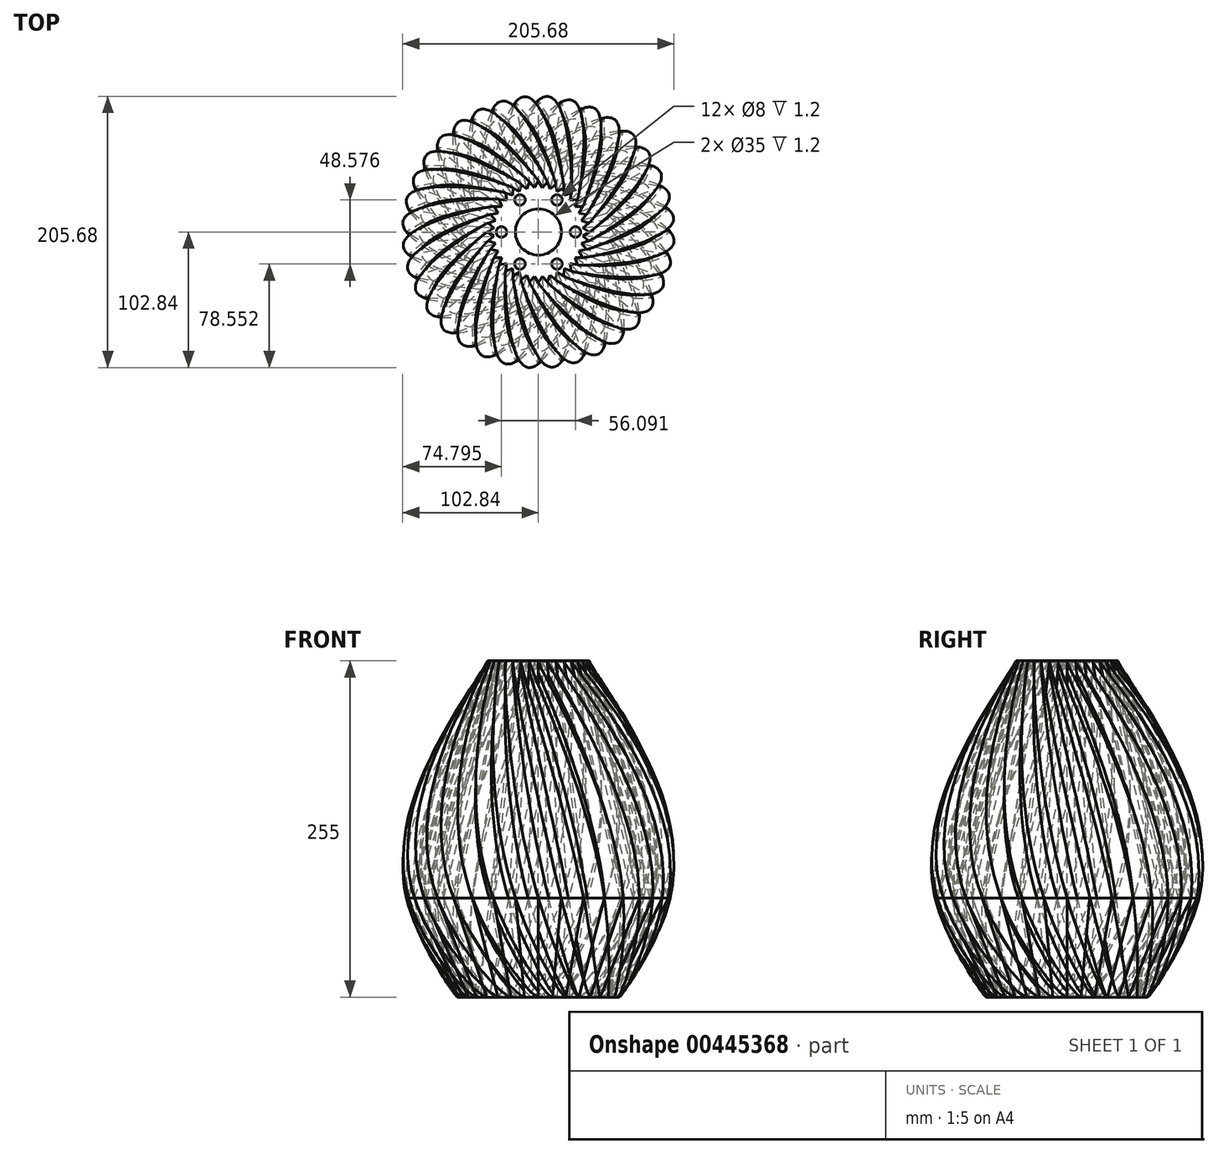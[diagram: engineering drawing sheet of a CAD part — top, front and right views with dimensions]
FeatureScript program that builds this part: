
annotation { "Feature Type Name" : "Feature", "Feature Type Description" : "" }
export const myFeature = defineFeature(function(context is Context, id is Id, definition is map)
    precondition{}
    {
        {
            var Q0;
            Q0=qCreatedBy(makeId("Top.planeOp"),FACE);
            var sketch = newSketch(context, id + "F0", { "sketchPlane" : qUnion([Q0])});
            skCircle(sketch, "E0", {"center": v(0, 0) * mm, "radius": 100 * mm, "construction": true});
            skLineSegment(sketch, "E1", {"start": v(-7.64, 87.34) * mm, "end": v(0, 100) * mm});
            skLineSegment(sketch, "E2.MirrorCS", {"start": v(7.64, 87.34) * mm, "end": v(0, 100) * mm});
            skLineSegment(sketch, "E3.1.0", {"start": v(-22.7, 84.69) * mm, "end": v(-17.36, 98.48) * mm});
            skLineSegment(sketch, "E3.1.1", {"start": v(-7.64, 87.34) * mm, "end": v(-17.36, 98.48) * mm});
            skLineSegment(sketch, "E3.2.0", {"start": v(-37.05, 79.46) * mm, "end": v(-34.2, 93.97) * mm});
            skLineSegment(sketch, "E3.2.1", {"start": v(-22.7, 84.69) * mm, "end": v(-34.2, 93.97) * mm});
            skLineSegment(sketch, "E3.3.0", {"start": v(-50.29, 71.82) * mm, "end": v(-50, 86.6) * mm});
            skLineSegment(sketch, "E3.3.1", {"start": v(-37.05, 79.46) * mm, "end": v(-50, 86.6) * mm});
            skLineSegment(sketch, "E3.4.0", {"start": v(-62, 62) * mm, "end": v(-64.28, 76.6) * mm});
            skLineSegment(sketch, "E3.4.1", {"start": v(-50.29, 71.82) * mm, "end": v(-64.28, 76.6) * mm});
            skLineSegment(sketch, "E3.5.0", {"start": v(-71.82, 50.29) * mm, "end": v(-76.6, 64.28) * mm});
            skLineSegment(sketch, "E3.5.1", {"start": v(-62, 62) * mm, "end": v(-76.6, 64.28) * mm});
            skLineSegment(sketch, "E3.6.0", {"start": v(-79.46, 37.05) * mm, "end": v(-86.6, 50) * mm});
            skLineSegment(sketch, "E3.6.1", {"start": v(-71.82, 50.29) * mm, "end": v(-86.6, 50) * mm});
            skLineSegment(sketch, "E3.7.0", {"start": v(-84.69, 22.7) * mm, "end": v(-93.97, 34.2) * mm});
            skLineSegment(sketch, "E3.7.1", {"start": v(-79.46, 37.05) * mm, "end": v(-93.97, 34.2) * mm});
            skLineSegment(sketch, "E3.8.0", {"start": v(-87.34, 7.64) * mm, "end": v(-98.48, 17.36) * mm});
            skLineSegment(sketch, "E3.8.1", {"start": v(-84.69, 22.7) * mm, "end": v(-98.48, 17.36) * mm});
            skLineSegment(sketch, "E3.9.0", {"start": v(-87.34, -7.64) * mm, "end": v(-100, 0) * mm});
            skLineSegment(sketch, "E3.9.1", {"start": v(-87.34, 7.64) * mm, "end": v(-100, 0) * mm});
            skLineSegment(sketch, "E3.10.0", {"start": v(-84.69, -22.7) * mm, "end": v(-98.48, -17.36) * mm});
            skLineSegment(sketch, "E3.10.1", {"start": v(-87.34, -7.64) * mm, "end": v(-98.48, -17.36) * mm});
            skLineSegment(sketch, "E3.11.0", {"start": v(-79.46, -37.05) * mm, "end": v(-93.97, -34.2) * mm});
            skLineSegment(sketch, "E3.11.1", {"start": v(-84.69, -22.7) * mm, "end": v(-93.97, -34.2) * mm});
            skLineSegment(sketch, "E3.12.0", {"start": v(-71.82, -50.29) * mm, "end": v(-86.6, -50) * mm});
            skLineSegment(sketch, "E3.12.1", {"start": v(-79.46, -37.05) * mm, "end": v(-86.6, -50) * mm});
            skLineSegment(sketch, "E3.13.0", {"start": v(-62, -62) * mm, "end": v(-76.6, -64.28) * mm});
            skLineSegment(sketch, "E3.13.1", {"start": v(-71.82, -50.29) * mm, "end": v(-76.6, -64.28) * mm});
            skLineSegment(sketch, "E3.14.0", {"start": v(-50.29, -71.82) * mm, "end": v(-64.28, -76.6) * mm});
            skLineSegment(sketch, "E3.14.1", {"start": v(-62, -62) * mm, "end": v(-64.28, -76.6) * mm});
            skLineSegment(sketch, "E3.15.0", {"start": v(-37.05, -79.46) * mm, "end": v(-50, -86.6) * mm});
            skLineSegment(sketch, "E3.15.1", {"start": v(-50.29, -71.82) * mm, "end": v(-50, -86.6) * mm});
            skLineSegment(sketch, "E3.16.0", {"start": v(-22.7, -84.69) * mm, "end": v(-34.2, -93.97) * mm});
            skLineSegment(sketch, "E3.16.1", {"start": v(-37.05, -79.46) * mm, "end": v(-34.2, -93.97) * mm});
            skLineSegment(sketch, "E3.17.0", {"start": v(-7.64, -87.34) * mm, "end": v(-17.36, -98.48) * mm});
            skLineSegment(sketch, "E3.17.1", {"start": v(-22.7, -84.69) * mm, "end": v(-17.36, -98.48) * mm});
            skLineSegment(sketch, "E3.18.0", {"start": v(7.64, -87.34) * mm, "end": v(0, -100) * mm});
            skLineSegment(sketch, "E3.18.1", {"start": v(-7.64, -87.34) * mm, "end": v(0, -100) * mm});
            skLineSegment(sketch, "E3.19.0", {"start": v(22.7, -84.69) * mm, "end": v(17.36, -98.48) * mm});
            skLineSegment(sketch, "E3.19.1", {"start": v(7.64, -87.34) * mm, "end": v(17.36, -98.48) * mm});
            skLineSegment(sketch, "E3.20.0", {"start": v(37.05, -79.46) * mm, "end": v(34.2, -93.97) * mm});
            skLineSegment(sketch, "E3.20.1", {"start": v(22.7, -84.69) * mm, "end": v(34.2, -93.97) * mm});
            skLineSegment(sketch, "E3.21.0", {"start": v(50.29, -71.82) * mm, "end": v(50, -86.6) * mm});
            skLineSegment(sketch, "E3.21.1", {"start": v(37.05, -79.46) * mm, "end": v(50, -86.6) * mm});
            skLineSegment(sketch, "E3.22.0", {"start": v(62, -62) * mm, "end": v(64.28, -76.6) * mm});
            skLineSegment(sketch, "E3.22.1", {"start": v(50.29, -71.82) * mm, "end": v(64.28, -76.6) * mm});
            skLineSegment(sketch, "E3.23.0", {"start": v(71.82, -50.29) * mm, "end": v(76.6, -64.28) * mm});
            skLineSegment(sketch, "E3.23.1", {"start": v(62, -62) * mm, "end": v(76.6, -64.28) * mm});
            skLineSegment(sketch, "E3.24.0", {"start": v(79.46, -37.05) * mm, "end": v(86.6, -50) * mm});
            skLineSegment(sketch, "E3.24.1", {"start": v(71.82, -50.29) * mm, "end": v(86.6, -50) * mm});
            skLineSegment(sketch, "E3.25.0", {"start": v(84.69, -22.7) * mm, "end": v(93.97, -34.2) * mm});
            skLineSegment(sketch, "E3.25.1", {"start": v(79.46, -37.05) * mm, "end": v(93.97, -34.2) * mm});
            skLineSegment(sketch, "E3.26.0", {"start": v(87.34, -7.64) * mm, "end": v(98.48, -17.36) * mm});
            skLineSegment(sketch, "E3.26.1", {"start": v(84.69, -22.7) * mm, "end": v(98.48, -17.36) * mm});
            skLineSegment(sketch, "E3.27.0", {"start": v(87.34, 7.64) * mm, "end": v(100, 0) * mm});
            skLineSegment(sketch, "E3.27.1", {"start": v(87.34, -7.64) * mm, "end": v(100, 0) * mm});
            skLineSegment(sketch, "E3.28.0", {"start": v(84.69, 22.7) * mm, "end": v(98.48, 17.36) * mm});
            skLineSegment(sketch, "E3.28.1", {"start": v(87.34, 7.64) * mm, "end": v(98.48, 17.36) * mm});
            skLineSegment(sketch, "E3.29.0", {"start": v(79.46, 37.05) * mm, "end": v(93.97, 34.2) * mm});
            skLineSegment(sketch, "E3.29.1", {"start": v(84.69, 22.7) * mm, "end": v(93.97, 34.2) * mm});
            skLineSegment(sketch, "E3.30.0", {"start": v(71.82, 50.29) * mm, "end": v(86.6, 50) * mm});
            skLineSegment(sketch, "E3.30.1", {"start": v(79.46, 37.05) * mm, "end": v(86.6, 50) * mm});
            skLineSegment(sketch, "E3.31.0", {"start": v(62, 62) * mm, "end": v(76.6, 64.28) * mm});
            skLineSegment(sketch, "E3.31.1", {"start": v(71.82, 50.29) * mm, "end": v(76.6, 64.28) * mm});
            skLineSegment(sketch, "E3.32.0", {"start": v(50.29, 71.82) * mm, "end": v(64.28, 76.6) * mm});
            skLineSegment(sketch, "E3.32.1", {"start": v(62, 62) * mm, "end": v(64.28, 76.6) * mm});
            skLineSegment(sketch, "E3.33.0", {"start": v(37.05, 79.46) * mm, "end": v(50, 86.6) * mm});
            skLineSegment(sketch, "E3.33.1", {"start": v(50.29, 71.82) * mm, "end": v(50, 86.6) * mm});
            skLineSegment(sketch, "E3.34.0", {"start": v(22.7, 84.69) * mm, "end": v(34.2, 93.97) * mm});
            skLineSegment(sketch, "E3.34.1", {"start": v(37.05, 79.46) * mm, "end": v(34.2, 93.97) * mm});
            skLineSegment(sketch, "E3.35.0", {"start": v(7.64, 87.34) * mm, "end": v(17.36, 98.48) * mm});
            skLineSegment(sketch, "E3.35.1", {"start": v(22.7, 84.69) * mm, "end": v(17.36, 98.48) * mm});
            skSolve(sketch);
        }
        {
            var Q0;
            Q0=makeQuery(id+"F0.imprint","IMPRINT",FACE,{"disambiguationData":[TD([[makeQuery(id+"F0.imprint","IMPRINT",EDGE,{"derivedFrom":sQuery(id+"F0.wireOp",EDGE,"E1")}),-1.0]])]});
            extrude(context, id + "F1", {"entities" : qUnion([Q0]), "depth" : 180 * mm, "hasDraft" : true, "draftAngle" : 10 * degree, "draftPullDirection" : true});
        }
        {
            var Q1;
            Q1=makeQuery(id+"F1.opExtrude","CAP_FACE",FACE,{"disambiguationData":[OSD([sQuery(id+"F0.wireOp",EDGE,"E1"),sQuery(id+"F0.wireOp",EDGE,"E2.MirrorCS"),sQuery(id+"F0.wireOp",EDGE,"E3.1.0"),sQuery(id+"F0.wireOp",EDGE,"E3.1.1"),sQuery(id+"F0.wireOp",EDGE,"E3.2.0"),sQuery(id+"F0.wireOp",EDGE,"E3.2.1"),sQuery(id+"F0.wireOp",EDGE,"E3.3.0"),sQuery(id+"F0.wireOp",EDGE,"E3.3.1"),sQuery(id+"F0.wireOp",EDGE,"E3.4.0"),sQuery(id+"F0.wireOp",EDGE,"E3.4.1"),sQuery(id+"F0.wireOp",EDGE,"E3.5.0"),sQuery(id+"F0.wireOp",EDGE,"E3.5.1"),sQuery(id+"F0.wireOp",EDGE,"E3.6.0"),sQuery(id+"F0.wireOp",EDGE,"E3.6.1"),sQuery(id+"F0.wireOp",EDGE,"E3.7.0"),sQuery(id+"F0.wireOp",EDGE,"E3.7.1"),sQuery(id+"F0.wireOp",EDGE,"E3.8.0"),sQuery(id+"F0.wireOp",EDGE,"E3.8.1"),sQuery(id+"F0.wireOp",EDGE,"E3.9.0"),sQuery(id+"F0.wireOp",EDGE,"E3.9.1"),sQuery(id+"F0.wireOp",EDGE,"E3.10.0"),sQuery(id+"F0.wireOp",EDGE,"E3.10.1"),sQuery(id+"F0.wireOp",EDGE,"E3.11.0"),sQuery(id+"F0.wireOp",EDGE,"E3.11.1"),sQuery(id+"F0.wireOp",EDGE,"E3.12.0"),sQuery(id+"F0.wireOp",EDGE,"E3.12.1"),sQuery(id+"F0.wireOp",EDGE,"E3.13.0"),sQuery(id+"F0.wireOp",EDGE,"E3.13.1"),sQuery(id+"F0.wireOp",EDGE,"E3.14.0"),sQuery(id+"F0.wireOp",EDGE,"E3.14.1"),sQuery(id+"F0.wireOp",EDGE,"E3.15.0"),sQuery(id+"F0.wireOp",EDGE,"E3.15.1"),sQuery(id+"F0.wireOp",EDGE,"E3.16.0"),sQuery(id+"F0.wireOp",EDGE,"E3.16.1"),sQuery(id+"F0.wireOp",EDGE,"E3.17.0"),sQuery(id+"F0.wireOp",EDGE,"E3.17.1"),sQuery(id+"F0.wireOp",EDGE,"E3.18.0"),sQuery(id+"F0.wireOp",EDGE,"E3.18.1"),sQuery(id+"F0.wireOp",EDGE,"E3.19.0"),sQuery(id+"F0.wireOp",EDGE,"E3.19.1"),sQuery(id+"F0.wireOp",EDGE,"E3.20.0"),sQuery(id+"F0.wireOp",EDGE,"E3.20.1"),sQuery(id+"F0.wireOp",EDGE,"E3.21.0"),sQuery(id+"F0.wireOp",EDGE,"E3.21.1"),sQuery(id+"F0.wireOp",EDGE,"E3.22.0"),sQuery(id+"F0.wireOp",EDGE,"E3.22.1"),sQuery(id+"F0.wireOp",EDGE,"E3.23.0"),sQuery(id+"F0.wireOp",EDGE,"E3.23.1"),sQuery(id+"F0.wireOp",EDGE,"E3.24.0"),sQuery(id+"F0.wireOp",EDGE,"E3.24.1"),sQuery(id+"F0.wireOp",EDGE,"E3.25.0"),sQuery(id+"F0.wireOp",EDGE,"E3.25.1"),sQuery(id+"F0.wireOp",EDGE,"E3.26.0"),sQuery(id+"F0.wireOp",EDGE,"E3.26.1"),sQuery(id+"F0.wireOp",EDGE,"E3.27.0"),sQuery(id+"F0.wireOp",EDGE,"E3.27.1"),sQuery(id+"F0.wireOp",EDGE,"E3.28.0"),sQuery(id+"F0.wireOp",EDGE,"E3.28.1"),sQuery(id+"F0.wireOp",EDGE,"E3.29.0"),sQuery(id+"F0.wireOp",EDGE,"E3.29.1"),sQuery(id+"F0.wireOp",EDGE,"E3.30.0"),sQuery(id+"F0.wireOp",EDGE,"E3.30.1"),sQuery(id+"F0.wireOp",EDGE,"E3.31.0"),sQuery(id+"F0.wireOp",EDGE,"E3.31.1"),sQuery(id+"F0.wireOp",EDGE,"E3.32.0"),sQuery(id+"F0.wireOp",EDGE,"E3.32.1"),sQuery(id+"F0.wireOp",EDGE,"E3.33.0"),sQuery(id+"F0.wireOp",EDGE,"E3.33.1"),sQuery(id+"F0.wireOp",EDGE,"E3.34.0"),sQuery(id+"F0.wireOp",EDGE,"E3.34.1"),sQuery(id+"F0.wireOp",EDGE,"E3.35.0"),sQuery(id+"F0.wireOp",EDGE,"E3.35.1")])],"isStart":false});
            var Q2;
            Q2=makeQuery(id+"F1.opExtrude","CAP_FACE",FACE,{"disambiguationData":[OSD([sQuery(id+"F0.wireOp",EDGE,"E1"),sQuery(id+"F0.wireOp",EDGE,"E2.MirrorCS"),sQuery(id+"F0.wireOp",EDGE,"E3.1.0"),sQuery(id+"F0.wireOp",EDGE,"E3.1.1"),sQuery(id+"F0.wireOp",EDGE,"E3.2.0"),sQuery(id+"F0.wireOp",EDGE,"E3.2.1"),sQuery(id+"F0.wireOp",EDGE,"E3.3.0"),sQuery(id+"F0.wireOp",EDGE,"E3.3.1"),sQuery(id+"F0.wireOp",EDGE,"E3.4.0"),sQuery(id+"F0.wireOp",EDGE,"E3.4.1"),sQuery(id+"F0.wireOp",EDGE,"E3.5.0"),sQuery(id+"F0.wireOp",EDGE,"E3.5.1"),sQuery(id+"F0.wireOp",EDGE,"E3.6.0"),sQuery(id+"F0.wireOp",EDGE,"E3.6.1"),sQuery(id+"F0.wireOp",EDGE,"E3.7.0"),sQuery(id+"F0.wireOp",EDGE,"E3.7.1"),sQuery(id+"F0.wireOp",EDGE,"E3.8.0"),sQuery(id+"F0.wireOp",EDGE,"E3.8.1"),sQuery(id+"F0.wireOp",EDGE,"E3.9.0"),sQuery(id+"F0.wireOp",EDGE,"E3.9.1"),sQuery(id+"F0.wireOp",EDGE,"E3.10.0"),sQuery(id+"F0.wireOp",EDGE,"E3.10.1"),sQuery(id+"F0.wireOp",EDGE,"E3.11.0"),sQuery(id+"F0.wireOp",EDGE,"E3.11.1"),sQuery(id+"F0.wireOp",EDGE,"E3.12.0"),sQuery(id+"F0.wireOp",EDGE,"E3.12.1"),sQuery(id+"F0.wireOp",EDGE,"E3.13.0"),sQuery(id+"F0.wireOp",EDGE,"E3.13.1"),sQuery(id+"F0.wireOp",EDGE,"E3.14.0"),sQuery(id+"F0.wireOp",EDGE,"E3.14.1"),sQuery(id+"F0.wireOp",EDGE,"E3.15.0"),sQuery(id+"F0.wireOp",EDGE,"E3.15.1"),sQuery(id+"F0.wireOp",EDGE,"E3.16.0"),sQuery(id+"F0.wireOp",EDGE,"E3.16.1"),sQuery(id+"F0.wireOp",EDGE,"E3.17.0"),sQuery(id+"F0.wireOp",EDGE,"E3.17.1"),sQuery(id+"F0.wireOp",EDGE,"E3.18.0"),sQuery(id+"F0.wireOp",EDGE,"E3.18.1"),sQuery(id+"F0.wireOp",EDGE,"E3.19.0"),sQuery(id+"F0.wireOp",EDGE,"E3.19.1"),sQuery(id+"F0.wireOp",EDGE,"E3.20.0"),sQuery(id+"F0.wireOp",EDGE,"E3.20.1"),sQuery(id+"F0.wireOp",EDGE,"E3.21.0"),sQuery(id+"F0.wireOp",EDGE,"E3.21.1"),sQuery(id+"F0.wireOp",EDGE,"E3.22.0"),sQuery(id+"F0.wireOp",EDGE,"E3.22.1"),sQuery(id+"F0.wireOp",EDGE,"E3.23.0"),sQuery(id+"F0.wireOp",EDGE,"E3.23.1"),sQuery(id+"F0.wireOp",EDGE,"E3.24.0"),sQuery(id+"F0.wireOp",EDGE,"E3.24.1"),sQuery(id+"F0.wireOp",EDGE,"E3.25.0"),sQuery(id+"F0.wireOp",EDGE,"E3.25.1"),sQuery(id+"F0.wireOp",EDGE,"E3.26.0"),sQuery(id+"F0.wireOp",EDGE,"E3.26.1"),sQuery(id+"F0.wireOp",EDGE,"E3.27.0"),sQuery(id+"F0.wireOp",EDGE,"E3.27.1"),sQuery(id+"F0.wireOp",EDGE,"E3.28.0"),sQuery(id+"F0.wireOp",EDGE,"E3.28.1"),sQuery(id+"F0.wireOp",EDGE,"E3.29.0"),sQuery(id+"F0.wireOp",EDGE,"E3.29.1"),sQuery(id+"F0.wireOp",EDGE,"E3.30.0"),sQuery(id+"F0.wireOp",EDGE,"E3.30.1"),sQuery(id+"F0.wireOp",EDGE,"E3.31.0"),sQuery(id+"F0.wireOp",EDGE,"E3.31.1"),sQuery(id+"F0.wireOp",EDGE,"E3.32.0"),sQuery(id+"F0.wireOp",EDGE,"E3.32.1"),sQuery(id+"F0.wireOp",EDGE,"E3.33.0"),sQuery(id+"F0.wireOp",EDGE,"E3.33.1"),sQuery(id+"F0.wireOp",EDGE,"E3.34.0"),sQuery(id+"F0.wireOp",EDGE,"E3.34.1"),sQuery(id+"F0.wireOp",EDGE,"E3.35.0"),sQuery(id+"F0.wireOp",EDGE,"E3.35.1")])],"isStart":true});
            var Q3;
            Q3=makeQuery(id+"F1.opExtrude","CAP_VERTEX",VERTEX,{"disambiguationData":[OSD([sQuery(id+"F0.wireOp",EDGE,"E3.18.0"),sQuery(id+"F0.wireOp",EDGE,"E3.18.1")])],"isStart":true});
            var Q4;
            Q4=makeQuery(id+"F1.opExtrude","CAP_VERTEX",VERTEX,{"disambiguationData":[OSD([sQuery(id+"F0.wireOp",EDGE,"E3.22.0"),sQuery(id+"F0.wireOp",EDGE,"E3.22.1")])],"isStart":false});
            loft(context, id + "F2", {"endCondition" : LoftEndDerivativeType.NORMAL_TO_PROFILE, "endMagnitude" : 2, "sheetProfilesArray" : [{ "sheetProfileEntities" : qUnion([Q1]) }, { "sheetProfileEntities" : qUnion([Q2]) }], "matchConnections" : true, "connections" : [{ "connectionEntities" : qUnion([Q3, Q4]), "connectionEdgeQueries" : qUnion([]), "connectionEdgeParameters" : [] }]});
        }
        {
            var Q0;
            Q0=makeQuery(id+"F2.opLoft","SWEPT_BODY",BODY,{"disambiguationData":[OSD([sQuery(id+"F0.wireOp",EDGE,"E1"),sQuery(id+"F0.wireOp",EDGE,"E2.MirrorCS"),sQuery(id+"F0.wireOp",EDGE,"E3.1.0"),sQuery(id+"F0.wireOp",EDGE,"E3.1.1"),sQuery(id+"F0.wireOp",EDGE,"E3.2.0"),sQuery(id+"F0.wireOp",EDGE,"E3.2.1"),sQuery(id+"F0.wireOp",EDGE,"E3.3.0"),sQuery(id+"F0.wireOp",EDGE,"E3.3.1"),sQuery(id+"F0.wireOp",EDGE,"E3.4.0"),sQuery(id+"F0.wireOp",EDGE,"E3.4.1"),sQuery(id+"F0.wireOp",EDGE,"E3.5.0"),sQuery(id+"F0.wireOp",EDGE,"E3.5.1"),sQuery(id+"F0.wireOp",EDGE,"E3.6.0"),sQuery(id+"F0.wireOp",EDGE,"E3.6.1"),sQuery(id+"F0.wireOp",EDGE,"E3.7.0"),sQuery(id+"F0.wireOp",EDGE,"E3.7.1"),sQuery(id+"F0.wireOp",EDGE,"E3.8.0"),sQuery(id+"F0.wireOp",EDGE,"E3.8.1"),sQuery(id+"F0.wireOp",EDGE,"E3.9.0"),sQuery(id+"F0.wireOp",EDGE,"E3.9.1"),sQuery(id+"F0.wireOp",EDGE,"E3.10.0"),sQuery(id+"F0.wireOp",EDGE,"E3.10.1"),sQuery(id+"F0.wireOp",EDGE,"E3.11.0"),sQuery(id+"F0.wireOp",EDGE,"E3.11.1"),sQuery(id+"F0.wireOp",EDGE,"E3.12.0"),sQuery(id+"F0.wireOp",EDGE,"E3.12.1"),sQuery(id+"F0.wireOp",EDGE,"E3.13.0"),sQuery(id+"F0.wireOp",EDGE,"E3.13.1"),sQuery(id+"F0.wireOp",EDGE,"E3.14.0"),sQuery(id+"F0.wireOp",EDGE,"E3.14.1"),sQuery(id+"F0.wireOp",EDGE,"E3.15.0"),sQuery(id+"F0.wireOp",EDGE,"E3.15.1"),sQuery(id+"F0.wireOp",EDGE,"E3.16.0"),sQuery(id+"F0.wireOp",EDGE,"E3.16.1"),sQuery(id+"F0.wireOp",EDGE,"E3.17.0"),sQuery(id+"F0.wireOp",EDGE,"E3.17.1"),sQuery(id+"F0.wireOp",EDGE,"E3.18.0"),sQuery(id+"F0.wireOp",EDGE,"E3.18.1"),sQuery(id+"F0.wireOp",EDGE,"E3.19.0"),sQuery(id+"F0.wireOp",EDGE,"E3.19.1"),sQuery(id+"F0.wireOp",EDGE,"E3.20.0"),sQuery(id+"F0.wireOp",EDGE,"E3.20.1"),sQuery(id+"F0.wireOp",EDGE,"E3.21.0"),sQuery(id+"F0.wireOp",EDGE,"E3.21.1"),sQuery(id+"F0.wireOp",EDGE,"E3.22.0"),sQuery(id+"F0.wireOp",EDGE,"E3.22.1"),sQuery(id+"F0.wireOp",EDGE,"E3.23.0"),sQuery(id+"F0.wireOp",EDGE,"E3.23.1"),sQuery(id+"F0.wireOp",EDGE,"E3.24.0"),sQuery(id+"F0.wireOp",EDGE,"E3.24.1"),sQuery(id+"F0.wireOp",EDGE,"E3.25.0"),sQuery(id+"F0.wireOp",EDGE,"E3.25.1"),sQuery(id+"F0.wireOp",EDGE,"E3.26.0"),sQuery(id+"F0.wireOp",EDGE,"E3.26.1"),sQuery(id+"F0.wireOp",EDGE,"E3.27.0"),sQuery(id+"F0.wireOp",EDGE,"E3.27.1"),sQuery(id+"F0.wireOp",EDGE,"E3.28.0"),sQuery(id+"F0.wireOp",EDGE,"E3.28.1"),sQuery(id+"F0.wireOp",EDGE,"E3.29.0"),sQuery(id+"F0.wireOp",EDGE,"E3.29.1"),sQuery(id+"F0.wireOp",EDGE,"E3.30.0"),sQuery(id+"F0.wireOp",EDGE,"E3.30.1"),sQuery(id+"F0.wireOp",EDGE,"E3.31.0"),sQuery(id+"F0.wireOp",EDGE,"E3.31.1"),sQuery(id+"F0.wireOp",EDGE,"E3.32.0"),sQuery(id+"F0.wireOp",EDGE,"E3.32.1"),sQuery(id+"F0.wireOp",EDGE,"E3.33.0"),sQuery(id+"F0.wireOp",EDGE,"E3.33.1"),sQuery(id+"F0.wireOp",EDGE,"E3.34.0"),sQuery(id+"F0.wireOp",EDGE,"E3.34.1"),sQuery(id+"F0.wireOp",EDGE,"E3.35.0"),sQuery(id+"F0.wireOp",EDGE,"E3.35.1")])]});
            deleteBodies(context, id + "F3", {"entities" : qUnion([Q0])});
        }
        {
            var Q0;
            Q0=makeQuery(id+"F1.opExtrude","CAP_FACE",FACE,{"disambiguationData":[OSD([sQuery(id+"F0.wireOp",EDGE,"E1"),sQuery(id+"F0.wireOp",EDGE,"E2.MirrorCS"),sQuery(id+"F0.wireOp",EDGE,"E3.1.0"),sQuery(id+"F0.wireOp",EDGE,"E3.1.1"),sQuery(id+"F0.wireOp",EDGE,"E3.2.0"),sQuery(id+"F0.wireOp",EDGE,"E3.2.1"),sQuery(id+"F0.wireOp",EDGE,"E3.3.0"),sQuery(id+"F0.wireOp",EDGE,"E3.3.1"),sQuery(id+"F0.wireOp",EDGE,"E3.4.0"),sQuery(id+"F0.wireOp",EDGE,"E3.4.1"),sQuery(id+"F0.wireOp",EDGE,"E3.5.0"),sQuery(id+"F0.wireOp",EDGE,"E3.5.1"),sQuery(id+"F0.wireOp",EDGE,"E3.6.0"),sQuery(id+"F0.wireOp",EDGE,"E3.6.1"),sQuery(id+"F0.wireOp",EDGE,"E3.7.0"),sQuery(id+"F0.wireOp",EDGE,"E3.7.1"),sQuery(id+"F0.wireOp",EDGE,"E3.8.0"),sQuery(id+"F0.wireOp",EDGE,"E3.8.1"),sQuery(id+"F0.wireOp",EDGE,"E3.9.0"),sQuery(id+"F0.wireOp",EDGE,"E3.9.1"),sQuery(id+"F0.wireOp",EDGE,"E3.10.0"),sQuery(id+"F0.wireOp",EDGE,"E3.10.1"),sQuery(id+"F0.wireOp",EDGE,"E3.11.0"),sQuery(id+"F0.wireOp",EDGE,"E3.11.1"),sQuery(id+"F0.wireOp",EDGE,"E3.12.0"),sQuery(id+"F0.wireOp",EDGE,"E3.12.1"),sQuery(id+"F0.wireOp",EDGE,"E3.13.0"),sQuery(id+"F0.wireOp",EDGE,"E3.13.1"),sQuery(id+"F0.wireOp",EDGE,"E3.14.0"),sQuery(id+"F0.wireOp",EDGE,"E3.14.1"),sQuery(id+"F0.wireOp",EDGE,"E3.15.0"),sQuery(id+"F0.wireOp",EDGE,"E3.15.1"),sQuery(id+"F0.wireOp",EDGE,"E3.16.0"),sQuery(id+"F0.wireOp",EDGE,"E3.16.1"),sQuery(id+"F0.wireOp",EDGE,"E3.17.0"),sQuery(id+"F0.wireOp",EDGE,"E3.17.1"),sQuery(id+"F0.wireOp",EDGE,"E3.18.0"),sQuery(id+"F0.wireOp",EDGE,"E3.18.1"),sQuery(id+"F0.wireOp",EDGE,"E3.19.0"),sQuery(id+"F0.wireOp",EDGE,"E3.19.1"),sQuery(id+"F0.wireOp",EDGE,"E3.20.0"),sQuery(id+"F0.wireOp",EDGE,"E3.20.1"),sQuery(id+"F0.wireOp",EDGE,"E3.21.0"),sQuery(id+"F0.wireOp",EDGE,"E3.21.1"),sQuery(id+"F0.wireOp",EDGE,"E3.22.0"),sQuery(id+"F0.wireOp",EDGE,"E3.22.1"),sQuery(id+"F0.wireOp",EDGE,"E3.23.0"),sQuery(id+"F0.wireOp",EDGE,"E3.23.1"),sQuery(id+"F0.wireOp",EDGE,"E3.24.0"),sQuery(id+"F0.wireOp",EDGE,"E3.24.1"),sQuery(id+"F0.wireOp",EDGE,"E3.25.0"),sQuery(id+"F0.wireOp",EDGE,"E3.25.1"),sQuery(id+"F0.wireOp",EDGE,"E3.26.0"),sQuery(id+"F0.wireOp",EDGE,"E3.26.1"),sQuery(id+"F0.wireOp",EDGE,"E3.27.0"),sQuery(id+"F0.wireOp",EDGE,"E3.27.1"),sQuery(id+"F0.wireOp",EDGE,"E3.28.0"),sQuery(id+"F0.wireOp",EDGE,"E3.28.1"),sQuery(id+"F0.wireOp",EDGE,"E3.29.0"),sQuery(id+"F0.wireOp",EDGE,"E3.29.1"),sQuery(id+"F0.wireOp",EDGE,"E3.30.0"),sQuery(id+"F0.wireOp",EDGE,"E3.30.1"),sQuery(id+"F0.wireOp",EDGE,"E3.31.0"),sQuery(id+"F0.wireOp",EDGE,"E3.31.1"),sQuery(id+"F0.wireOp",EDGE,"E3.32.0"),sQuery(id+"F0.wireOp",EDGE,"E3.32.1"),sQuery(id+"F0.wireOp",EDGE,"E3.33.0"),sQuery(id+"F0.wireOp",EDGE,"E3.33.1"),sQuery(id+"F0.wireOp",EDGE,"E3.34.0"),sQuery(id+"F0.wireOp",EDGE,"E3.34.1"),sQuery(id+"F0.wireOp",EDGE,"E3.35.0"),sQuery(id+"F0.wireOp",EDGE,"E3.35.1")])],"isStart":true});
            extrude(context, id + "F4", {"entities" : qUnion([Q0]), "depth" : 75 * mm, "hasDraft" : true, "draftAngle" : 15 * degree, "draftPullDirection" : true});
        }
        {
            var Q1;
            Q1=makeQuery(id+"F1.opExtrude","CAP_FACE",FACE,{"disambiguationData":[OSD([sQuery(id+"F0.wireOp",EDGE,"E1"),sQuery(id+"F0.wireOp",EDGE,"E2.MirrorCS"),sQuery(id+"F0.wireOp",EDGE,"E3.1.0"),sQuery(id+"F0.wireOp",EDGE,"E3.1.1"),sQuery(id+"F0.wireOp",EDGE,"E3.2.0"),sQuery(id+"F0.wireOp",EDGE,"E3.2.1"),sQuery(id+"F0.wireOp",EDGE,"E3.3.0"),sQuery(id+"F0.wireOp",EDGE,"E3.3.1"),sQuery(id+"F0.wireOp",EDGE,"E3.4.0"),sQuery(id+"F0.wireOp",EDGE,"E3.4.1"),sQuery(id+"F0.wireOp",EDGE,"E3.5.0"),sQuery(id+"F0.wireOp",EDGE,"E3.5.1"),sQuery(id+"F0.wireOp",EDGE,"E3.6.0"),sQuery(id+"F0.wireOp",EDGE,"E3.6.1"),sQuery(id+"F0.wireOp",EDGE,"E3.7.0"),sQuery(id+"F0.wireOp",EDGE,"E3.7.1"),sQuery(id+"F0.wireOp",EDGE,"E3.8.0"),sQuery(id+"F0.wireOp",EDGE,"E3.8.1"),sQuery(id+"F0.wireOp",EDGE,"E3.9.0"),sQuery(id+"F0.wireOp",EDGE,"E3.9.1"),sQuery(id+"F0.wireOp",EDGE,"E3.10.0"),sQuery(id+"F0.wireOp",EDGE,"E3.10.1"),sQuery(id+"F0.wireOp",EDGE,"E3.11.0"),sQuery(id+"F0.wireOp",EDGE,"E3.11.1"),sQuery(id+"F0.wireOp",EDGE,"E3.12.0"),sQuery(id+"F0.wireOp",EDGE,"E3.12.1"),sQuery(id+"F0.wireOp",EDGE,"E3.13.0"),sQuery(id+"F0.wireOp",EDGE,"E3.13.1"),sQuery(id+"F0.wireOp",EDGE,"E3.14.0"),sQuery(id+"F0.wireOp",EDGE,"E3.14.1"),sQuery(id+"F0.wireOp",EDGE,"E3.15.0"),sQuery(id+"F0.wireOp",EDGE,"E3.15.1"),sQuery(id+"F0.wireOp",EDGE,"E3.16.0"),sQuery(id+"F0.wireOp",EDGE,"E3.16.1"),sQuery(id+"F0.wireOp",EDGE,"E3.17.0"),sQuery(id+"F0.wireOp",EDGE,"E3.17.1"),sQuery(id+"F0.wireOp",EDGE,"E3.18.0"),sQuery(id+"F0.wireOp",EDGE,"E3.18.1"),sQuery(id+"F0.wireOp",EDGE,"E3.19.0"),sQuery(id+"F0.wireOp",EDGE,"E3.19.1"),sQuery(id+"F0.wireOp",EDGE,"E3.20.0"),sQuery(id+"F0.wireOp",EDGE,"E3.20.1"),sQuery(id+"F0.wireOp",EDGE,"E3.21.0"),sQuery(id+"F0.wireOp",EDGE,"E3.21.1"),sQuery(id+"F0.wireOp",EDGE,"E3.22.0"),sQuery(id+"F0.wireOp",EDGE,"E3.22.1"),sQuery(id+"F0.wireOp",EDGE,"E3.23.0"),sQuery(id+"F0.wireOp",EDGE,"E3.23.1"),sQuery(id+"F0.wireOp",EDGE,"E3.24.0"),sQuery(id+"F0.wireOp",EDGE,"E3.24.1"),sQuery(id+"F0.wireOp",EDGE,"E3.25.0"),sQuery(id+"F0.wireOp",EDGE,"E3.25.1"),sQuery(id+"F0.wireOp",EDGE,"E3.26.0"),sQuery(id+"F0.wireOp",EDGE,"E3.26.1"),sQuery(id+"F0.wireOp",EDGE,"E3.27.0"),sQuery(id+"F0.wireOp",EDGE,"E3.27.1"),sQuery(id+"F0.wireOp",EDGE,"E3.28.0"),sQuery(id+"F0.wireOp",EDGE,"E3.28.1"),sQuery(id+"F0.wireOp",EDGE,"E3.29.0"),sQuery(id+"F0.wireOp",EDGE,"E3.29.1"),sQuery(id+"F0.wireOp",EDGE,"E3.30.0"),sQuery(id+"F0.wireOp",EDGE,"E3.30.1"),sQuery(id+"F0.wireOp",EDGE,"E3.31.0"),sQuery(id+"F0.wireOp",EDGE,"E3.31.1"),sQuery(id+"F0.wireOp",EDGE,"E3.32.0"),sQuery(id+"F0.wireOp",EDGE,"E3.32.1"),sQuery(id+"F0.wireOp",EDGE,"E3.33.0"),sQuery(id+"F0.wireOp",EDGE,"E3.33.1"),sQuery(id+"F0.wireOp",EDGE,"E3.34.0"),sQuery(id+"F0.wireOp",EDGE,"E3.34.1"),sQuery(id+"F0.wireOp",EDGE,"E3.35.0"),sQuery(id+"F0.wireOp",EDGE,"E3.35.1")])],"isStart":false});
            var Q2;
            Q2=makeQuery(id+"F1.opExtrude","CAP_FACE",FACE,{"disambiguationData":[OSD([sQuery(id+"F0.wireOp",EDGE,"E1"),sQuery(id+"F0.wireOp",EDGE,"E2.MirrorCS"),sQuery(id+"F0.wireOp",EDGE,"E3.1.0"),sQuery(id+"F0.wireOp",EDGE,"E3.1.1"),sQuery(id+"F0.wireOp",EDGE,"E3.2.0"),sQuery(id+"F0.wireOp",EDGE,"E3.2.1"),sQuery(id+"F0.wireOp",EDGE,"E3.3.0"),sQuery(id+"F0.wireOp",EDGE,"E3.3.1"),sQuery(id+"F0.wireOp",EDGE,"E3.4.0"),sQuery(id+"F0.wireOp",EDGE,"E3.4.1"),sQuery(id+"F0.wireOp",EDGE,"E3.5.0"),sQuery(id+"F0.wireOp",EDGE,"E3.5.1"),sQuery(id+"F0.wireOp",EDGE,"E3.6.0"),sQuery(id+"F0.wireOp",EDGE,"E3.6.1"),sQuery(id+"F0.wireOp",EDGE,"E3.7.0"),sQuery(id+"F0.wireOp",EDGE,"E3.7.1"),sQuery(id+"F0.wireOp",EDGE,"E3.8.0"),sQuery(id+"F0.wireOp",EDGE,"E3.8.1"),sQuery(id+"F0.wireOp",EDGE,"E3.9.0"),sQuery(id+"F0.wireOp",EDGE,"E3.9.1"),sQuery(id+"F0.wireOp",EDGE,"E3.10.0"),sQuery(id+"F0.wireOp",EDGE,"E3.10.1"),sQuery(id+"F0.wireOp",EDGE,"E3.11.0"),sQuery(id+"F0.wireOp",EDGE,"E3.11.1"),sQuery(id+"F0.wireOp",EDGE,"E3.12.0"),sQuery(id+"F0.wireOp",EDGE,"E3.12.1"),sQuery(id+"F0.wireOp",EDGE,"E3.13.0"),sQuery(id+"F0.wireOp",EDGE,"E3.13.1"),sQuery(id+"F0.wireOp",EDGE,"E3.14.0"),sQuery(id+"F0.wireOp",EDGE,"E3.14.1"),sQuery(id+"F0.wireOp",EDGE,"E3.15.0"),sQuery(id+"F0.wireOp",EDGE,"E3.15.1"),sQuery(id+"F0.wireOp",EDGE,"E3.16.0"),sQuery(id+"F0.wireOp",EDGE,"E3.16.1"),sQuery(id+"F0.wireOp",EDGE,"E3.17.0"),sQuery(id+"F0.wireOp",EDGE,"E3.17.1"),sQuery(id+"F0.wireOp",EDGE,"E3.18.0"),sQuery(id+"F0.wireOp",EDGE,"E3.18.1"),sQuery(id+"F0.wireOp",EDGE,"E3.19.0"),sQuery(id+"F0.wireOp",EDGE,"E3.19.1"),sQuery(id+"F0.wireOp",EDGE,"E3.20.0"),sQuery(id+"F0.wireOp",EDGE,"E3.20.1"),sQuery(id+"F0.wireOp",EDGE,"E3.21.0"),sQuery(id+"F0.wireOp",EDGE,"E3.21.1"),sQuery(id+"F0.wireOp",EDGE,"E3.22.0"),sQuery(id+"F0.wireOp",EDGE,"E3.22.1"),sQuery(id+"F0.wireOp",EDGE,"E3.23.0"),sQuery(id+"F0.wireOp",EDGE,"E3.23.1"),sQuery(id+"F0.wireOp",EDGE,"E3.24.0"),sQuery(id+"F0.wireOp",EDGE,"E3.24.1"),sQuery(id+"F0.wireOp",EDGE,"E3.25.0"),sQuery(id+"F0.wireOp",EDGE,"E3.25.1"),sQuery(id+"F0.wireOp",EDGE,"E3.26.0"),sQuery(id+"F0.wireOp",EDGE,"E3.26.1"),sQuery(id+"F0.wireOp",EDGE,"E3.27.0"),sQuery(id+"F0.wireOp",EDGE,"E3.27.1"),sQuery(id+"F0.wireOp",EDGE,"E3.28.0"),sQuery(id+"F0.wireOp",EDGE,"E3.28.1"),sQuery(id+"F0.wireOp",EDGE,"E3.29.0"),sQuery(id+"F0.wireOp",EDGE,"E3.29.1"),sQuery(id+"F0.wireOp",EDGE,"E3.30.0"),sQuery(id+"F0.wireOp",EDGE,"E3.30.1"),sQuery(id+"F0.wireOp",EDGE,"E3.31.0"),sQuery(id+"F0.wireOp",EDGE,"E3.31.1"),sQuery(id+"F0.wireOp",EDGE,"E3.32.0"),sQuery(id+"F0.wireOp",EDGE,"E3.32.1"),sQuery(id+"F0.wireOp",EDGE,"E3.33.0"),sQuery(id+"F0.wireOp",EDGE,"E3.33.1"),sQuery(id+"F0.wireOp",EDGE,"E3.34.0"),sQuery(id+"F0.wireOp",EDGE,"E3.34.1"),sQuery(id+"F0.wireOp",EDGE,"E3.35.0"),sQuery(id+"F0.wireOp",EDGE,"E3.35.1")])],"isStart":true});
            var Q3;
            Q3=makeQuery(id+"F4.opExtrude","CAP_FACE",FACE,{"disambiguationData":[OSD([sQuery(id+"F0.wireOp",EDGE,"E1"),sQuery(id+"F0.wireOp",EDGE,"E2.MirrorCS"),sQuery(id+"F0.wireOp",EDGE,"E3.1.0"),sQuery(id+"F0.wireOp",EDGE,"E3.1.1"),sQuery(id+"F0.wireOp",EDGE,"E3.2.0"),sQuery(id+"F0.wireOp",EDGE,"E3.2.1"),sQuery(id+"F0.wireOp",EDGE,"E3.3.0"),sQuery(id+"F0.wireOp",EDGE,"E3.3.1"),sQuery(id+"F0.wireOp",EDGE,"E3.4.0"),sQuery(id+"F0.wireOp",EDGE,"E3.4.1"),sQuery(id+"F0.wireOp",EDGE,"E3.5.0"),sQuery(id+"F0.wireOp",EDGE,"E3.5.1"),sQuery(id+"F0.wireOp",EDGE,"E3.6.0"),sQuery(id+"F0.wireOp",EDGE,"E3.6.1"),sQuery(id+"F0.wireOp",EDGE,"E3.7.0"),sQuery(id+"F0.wireOp",EDGE,"E3.7.1"),sQuery(id+"F0.wireOp",EDGE,"E3.8.0"),sQuery(id+"F0.wireOp",EDGE,"E3.8.1"),sQuery(id+"F0.wireOp",EDGE,"E3.9.0"),sQuery(id+"F0.wireOp",EDGE,"E3.9.1"),sQuery(id+"F0.wireOp",EDGE,"E3.10.0"),sQuery(id+"F0.wireOp",EDGE,"E3.10.1"),sQuery(id+"F0.wireOp",EDGE,"E3.11.0"),sQuery(id+"F0.wireOp",EDGE,"E3.11.1"),sQuery(id+"F0.wireOp",EDGE,"E3.12.0"),sQuery(id+"F0.wireOp",EDGE,"E3.12.1"),sQuery(id+"F0.wireOp",EDGE,"E3.13.0"),sQuery(id+"F0.wireOp",EDGE,"E3.13.1"),sQuery(id+"F0.wireOp",EDGE,"E3.14.0"),sQuery(id+"F0.wireOp",EDGE,"E3.14.1"),sQuery(id+"F0.wireOp",EDGE,"E3.15.0"),sQuery(id+"F0.wireOp",EDGE,"E3.15.1"),sQuery(id+"F0.wireOp",EDGE,"E3.16.0"),sQuery(id+"F0.wireOp",EDGE,"E3.16.1"),sQuery(id+"F0.wireOp",EDGE,"E3.17.0"),sQuery(id+"F0.wireOp",EDGE,"E3.17.1"),sQuery(id+"F0.wireOp",EDGE,"E3.18.0"),sQuery(id+"F0.wireOp",EDGE,"E3.18.1"),sQuery(id+"F0.wireOp",EDGE,"E3.19.0"),sQuery(id+"F0.wireOp",EDGE,"E3.19.1"),sQuery(id+"F0.wireOp",EDGE,"E3.20.0"),sQuery(id+"F0.wireOp",EDGE,"E3.20.1"),sQuery(id+"F0.wireOp",EDGE,"E3.21.0"),sQuery(id+"F0.wireOp",EDGE,"E3.21.1"),sQuery(id+"F0.wireOp",EDGE,"E3.22.0"),sQuery(id+"F0.wireOp",EDGE,"E3.22.1"),sQuery(id+"F0.wireOp",EDGE,"E3.23.0"),sQuery(id+"F0.wireOp",EDGE,"E3.23.1"),sQuery(id+"F0.wireOp",EDGE,"E3.24.0"),sQuery(id+"F0.wireOp",EDGE,"E3.24.1"),sQuery(id+"F0.wireOp",EDGE,"E3.25.0"),sQuery(id+"F0.wireOp",EDGE,"E3.25.1"),sQuery(id+"F0.wireOp",EDGE,"E3.26.0"),sQuery(id+"F0.wireOp",EDGE,"E3.26.1"),sQuery(id+"F0.wireOp",EDGE,"E3.27.0"),sQuery(id+"F0.wireOp",EDGE,"E3.27.1"),sQuery(id+"F0.wireOp",EDGE,"E3.28.0"),sQuery(id+"F0.wireOp",EDGE,"E3.28.1"),sQuery(id+"F0.wireOp",EDGE,"E3.29.0"),sQuery(id+"F0.wireOp",EDGE,"E3.29.1"),sQuery(id+"F0.wireOp",EDGE,"E3.30.0"),sQuery(id+"F0.wireOp",EDGE,"E3.30.1"),sQuery(id+"F0.wireOp",EDGE,"E3.31.0"),sQuery(id+"F0.wireOp",EDGE,"E3.31.1"),sQuery(id+"F0.wireOp",EDGE,"E3.32.0"),sQuery(id+"F0.wireOp",EDGE,"E3.32.1"),sQuery(id+"F0.wireOp",EDGE,"E3.33.0"),sQuery(id+"F0.wireOp",EDGE,"E3.33.1"),sQuery(id+"F0.wireOp",EDGE,"E3.34.0"),sQuery(id+"F0.wireOp",EDGE,"E3.34.1"),sQuery(id+"F0.wireOp",EDGE,"E3.35.0"),sQuery(id+"F0.wireOp",EDGE,"E3.35.1")])],"isStart":false});
            var Q4;
            Q4=makeQuery(id+"F1.opExtrude","CAP_VERTEX",VERTEX,{"disambiguationData":[OSD([sQuery(id+"F0.wireOp",EDGE,"E3.18.0"),sQuery(id+"F0.wireOp",EDGE,"E3.18.1")])],"isStart":false});
            var Q5;
            Q5=makeQuery(id+"F1.opExtrude","CAP_VERTEX",VERTEX,{"disambiguationData":[OSD([sQuery(id+"F0.wireOp",EDGE,"E3.22.0"),sQuery(id+"F0.wireOp",EDGE,"E3.22.1")])],"isStart":true});
            var Q6;
            Q6=makeQuery(id+"F4.opExtrude","CAP_VERTEX",VERTEX,{"disambiguationData":[OSD([sQuery(id+"F0.wireOp",EDGE,"E3.25.0"),sQuery(id+"F0.wireOp",EDGE,"E3.25.1")])],"isStart":false});
            loft(context, id + "F5", {"startCondition" : LoftEndDerivativeType.MATCH_TANGENT, "startMagnitude" : .1, "endCondition" : LoftEndDerivativeType.TANGENT_TO_PROFILE, "endMagnitude" : .25, "sheetProfilesArray" : [{ "sheetProfileEntities" : qUnion([Q1]) }, { "sheetProfileEntities" : qUnion([Q2]) }, { "sheetProfileEntities" : qUnion([Q3]) }], "matchConnections" : true, "connections" : [{ "connectionEntities" : qUnion([Q4, Q5, Q6]), "connectionEdgeQueries" : qUnion([]), "connectionEdgeParameters" : [] }]});
        }
        {
            var Q0;
            {var subQ0=sQuery(id+"F0.wireOp",EDGE,"E3.35.1");var subQ1=sQuery(id+"F0.wireOp",EDGE,"E3.35.0");var subQ2=sQuery(id+"F0.wireOp",EDGE,"E3.34.1");var subQ3=sQuery(id+"F0.wireOp",EDGE,"E3.34.0");var subQ4=sQuery(id+"F0.wireOp",EDGE,"E3.33.1");var subQ5=sQuery(id+"F0.wireOp",EDGE,"E3.33.0");var subQ6=sQuery(id+"F0.wireOp",EDGE,"E3.32.1");var subQ7=sQuery(id+"F0.wireOp",EDGE,"E3.32.0");var subQ8=sQuery(id+"F0.wireOp",EDGE,"E3.31.1");var subQ9=sQuery(id+"F0.wireOp",EDGE,"E3.31.0");var subQ10=sQuery(id+"F0.wireOp",EDGE,"E3.30.1");var subQ11=sQuery(id+"F0.wireOp",EDGE,"E3.30.0");var subQ12=sQuery(id+"F0.wireOp",EDGE,"E3.29.1");var subQ13=sQuery(id+"F0.wireOp",EDGE,"E3.29.0");var subQ14=sQuery(id+"F0.wireOp",EDGE,"E3.28.1");var subQ15=sQuery(id+"F0.wireOp",EDGE,"E3.28.0");var subQ16=sQuery(id+"F0.wireOp",EDGE,"E3.27.1");var subQ17=sQuery(id+"F0.wireOp",EDGE,"E3.27.0");var subQ18=sQuery(id+"F0.wireOp",EDGE,"E3.26.1");var subQ19=sQuery(id+"F0.wireOp",EDGE,"E3.26.0");var subQ20=sQuery(id+"F0.wireOp",EDGE,"E3.25.1");var subQ21=sQuery(id+"F0.wireOp",EDGE,"E3.25.0");var subQ22=sQuery(id+"F0.wireOp",EDGE,"E3.24.1");var subQ23=sQuery(id+"F0.wireOp",EDGE,"E3.24.0");var subQ24=sQuery(id+"F0.wireOp",EDGE,"E3.23.1");var subQ25=sQuery(id+"F0.wireOp",EDGE,"E3.23.0");var subQ26=sQuery(id+"F0.wireOp",EDGE,"E3.22.1");var subQ27=sQuery(id+"F0.wireOp",EDGE,"E3.22.0");var subQ28=sQuery(id+"F0.wireOp",EDGE,"E3.21.1");var subQ29=sQuery(id+"F0.wireOp",EDGE,"E3.21.0");var subQ30=sQuery(id+"F0.wireOp",EDGE,"E3.20.1");var subQ31=sQuery(id+"F0.wireOp",EDGE,"E3.20.0");var subQ32=sQuery(id+"F0.wireOp",EDGE,"E3.19.1");var subQ33=sQuery(id+"F0.wireOp",EDGE,"E3.19.0");var subQ34=sQuery(id+"F0.wireOp",EDGE,"E3.18.1");var subQ35=sQuery(id+"F0.wireOp",EDGE,"E3.18.0");var subQ36=sQuery(id+"F0.wireOp",EDGE,"E3.17.1");var subQ37=sQuery(id+"F0.wireOp",EDGE,"E3.17.0");var subQ38=sQuery(id+"F0.wireOp",EDGE,"E3.16.1");var subQ39=sQuery(id+"F0.wireOp",EDGE,"E3.16.0");var subQ40=sQuery(id+"F0.wireOp",EDGE,"E3.15.1");var subQ41=sQuery(id+"F0.wireOp",EDGE,"E3.15.0");var subQ42=sQuery(id+"F0.wireOp",EDGE,"E3.14.1");var subQ43=sQuery(id+"F0.wireOp",EDGE,"E3.14.0");var subQ44=sQuery(id+"F0.wireOp",EDGE,"E3.13.1");var subQ45=sQuery(id+"F0.wireOp",EDGE,"E3.13.0");var subQ46=sQuery(id+"F0.wireOp",EDGE,"E3.12.1");var subQ47=sQuery(id+"F0.wireOp",EDGE,"E3.12.0");var subQ48=sQuery(id+"F0.wireOp",EDGE,"E3.11.1");var subQ49=sQuery(id+"F0.wireOp",EDGE,"E3.11.0");var subQ50=sQuery(id+"F0.wireOp",EDGE,"E3.10.1");var subQ51=sQuery(id+"F0.wireOp",EDGE,"E3.10.0");var subQ52=sQuery(id+"F0.wireOp",EDGE,"E3.9.1");var subQ53=sQuery(id+"F0.wireOp",EDGE,"E3.9.0");var subQ54=sQuery(id+"F0.wireOp",EDGE,"E3.8.1");var subQ55=sQuery(id+"F0.wireOp",EDGE,"E3.8.0");var subQ56=sQuery(id+"F0.wireOp",EDGE,"E3.7.1");var subQ57=sQuery(id+"F0.wireOp",EDGE,"E3.7.0");var subQ58=sQuery(id+"F0.wireOp",EDGE,"E3.6.1");var subQ59=sQuery(id+"F0.wireOp",EDGE,"E3.6.0");var subQ60=sQuery(id+"F0.wireOp",EDGE,"E3.5.1");var subQ61=sQuery(id+"F0.wireOp",EDGE,"E3.5.0");var subQ62=sQuery(id+"F0.wireOp",EDGE,"E3.4.1");var subQ63=sQuery(id+"F0.wireOp",EDGE,"E3.4.0");var subQ64=sQuery(id+"F0.wireOp",EDGE,"E3.3.1");var subQ65=sQuery(id+"F0.wireOp",EDGE,"E3.3.0");var subQ66=sQuery(id+"F0.wireOp",EDGE,"E3.2.1");var subQ67=sQuery(id+"F0.wireOp",EDGE,"E3.2.0");var subQ68=sQuery(id+"F0.wireOp",EDGE,"E3.1.1");var subQ69=sQuery(id+"F0.wireOp",EDGE,"E3.1.0");var subQ70=sQuery(id+"F0.wireOp",EDGE,"E2.MirrorCS");var subQ71=sQuery(id+"F0.wireOp",EDGE,"E1");Q0=makeQuery(id+"F5.opLoft","CAP_FACE",FACE,{"disambiguationData":[OSD([subQ71,subQ70,subQ69,subQ68,subQ67,subQ66,subQ65,subQ64,subQ63,subQ62,subQ61,subQ60,subQ59,subQ58,subQ57,subQ56,subQ55,subQ54,subQ53,subQ52,subQ51,subQ50,subQ49,subQ48,subQ47,subQ46,subQ45,subQ44,subQ43,subQ42,subQ41,subQ40,subQ39,subQ38,subQ37,subQ36,subQ35,subQ34,subQ33,subQ32,subQ31,subQ30,subQ29,subQ28,subQ27,subQ26,subQ25,subQ24,subQ23,subQ22,subQ21,subQ20,subQ19,subQ18,subQ17,subQ16,subQ15,subQ14,subQ13,subQ12,subQ11,subQ10,subQ9,subQ8,subQ7,subQ6,subQ5,subQ4,subQ3,subQ2,subQ1,subQ0]),TDD([makeQuery(id+"F1.opExtrude","CAP_FACE",FACE,{"disambiguationData":[OSD([subQ71,subQ70,subQ69,subQ68,subQ67,subQ66,subQ65,subQ64,subQ63,subQ62,subQ61,subQ60,subQ59,subQ58,subQ57,subQ56,subQ55,subQ54,subQ53,subQ52,subQ51,subQ50,subQ49,subQ48,subQ47,subQ46,subQ45,subQ44,subQ43,subQ42,subQ41,subQ40,subQ39,subQ38,subQ37,subQ36,subQ35,subQ34,subQ33,subQ32,subQ31,subQ30,subQ29,subQ28,subQ27,subQ26,subQ25,subQ24,subQ23,subQ22,subQ21,subQ20,subQ19,subQ18,subQ17,subQ16,subQ15,subQ14,subQ13,subQ12,subQ11,subQ10,subQ9,subQ8,subQ7,subQ6,subQ5,subQ4,subQ3,subQ2,subQ1,subQ0])],"isStart":false})])],"isStart":true});}
            var sketch = newSketch(context, id + "F6", { "sketchPlane" : qUnion([Q0])});
            skCircle(sketch, "E4", {"center": v(0, 0) * mm, "radius": 17.5 * mm});
            skCircle(sketch, "E5", {"center": v(28.05, 0) * mm, "radius": 4 * mm});
            skLineSegment(sketch, "E6", {"start": v(38.6, 0) * mm, "end": v(17.5, 0) * mm, "construction": true});
            skCircle(sketch, "E7.1.0", {"center": v(14.02, 24.29) * mm, "radius": 4 * mm});
            skCircle(sketch, "E7.2.0", {"center": v(-14.02, 24.29) * mm, "radius": 4 * mm});
            skCircle(sketch, "E7.3.0", {"center": v(-28.05, 0) * mm, "radius": 4 * mm});
            skCircle(sketch, "E7.4.0", {"center": v(-14.02, -24.29) * mm, "radius": 4 * mm});
            skCircle(sketch, "E7.5.0", {"center": v(14.02, -24.29) * mm, "radius": 4 * mm});
            skSolve(sketch);
        }
        {
            var Q0;
            Q0=qSketchRegion(id+"F6",true);
            extrude(context, id + "F7", {"entities" : qUnion([Q0]), "operationType" : NewBodyOperationType.REMOVE, "oppositeDirection" : true, "depth" : 1.2 * mm});
        }
    });
